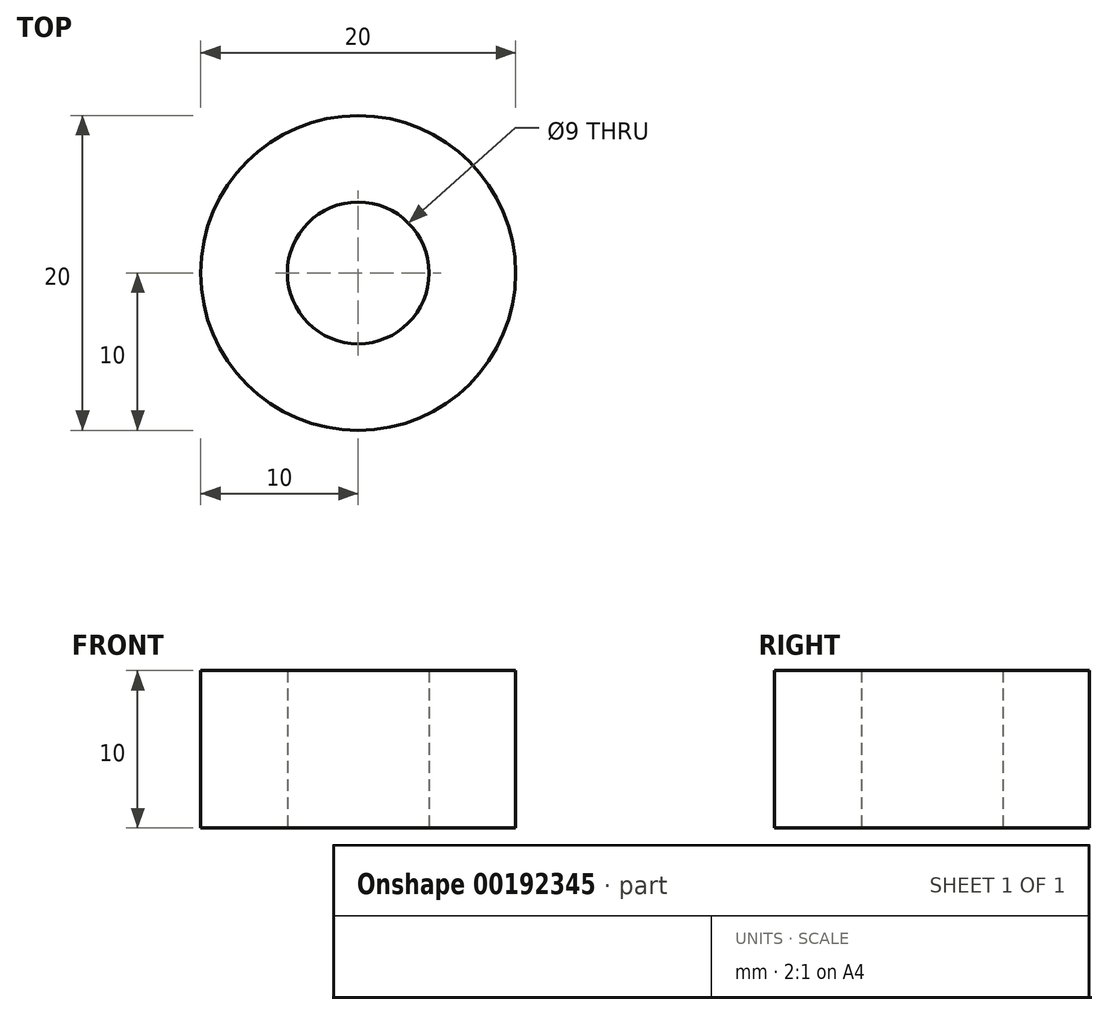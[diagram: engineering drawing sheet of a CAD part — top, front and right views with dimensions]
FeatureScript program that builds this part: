
annotation { "Feature Type Name" : "Feature", "Feature Type Description" : "" }
export const myFeature = defineFeature(function(context is Context, id is Id, definition is map)
    precondition{}
    {
        {
            var Q0;
            Q0=qCreatedBy(makeId("Top.planeOp"),FACE);
            var sketch = newSketch(context, id + "F0", { "sketchPlane" : qUnion([Q0])});
            skCircle(sketch, "E0", {"center": v(0, 0) * mm, "radius": 4.5 * mm});
            skCircle(sketch, "E1.0", {"center": v(0, 0) * mm, "radius": 10 * mm});
            skSolve(sketch);
        }
        {
            var Q0;
            Q0=makeQuery(id+"F0.imprint","IMPRINT",FACE,{"disambiguationData":[TD([[makeQuery(id+"F0.imprint","IMPRINT",EDGE,{"derivedFrom":sQuery(id+"F0.wireOp",EDGE,"E0")}),-1.0]])]});
            extrude(context, id + "F1", {"entities" : qUnion([Q0]), "depth" : 10 * mm});
        }
    });
